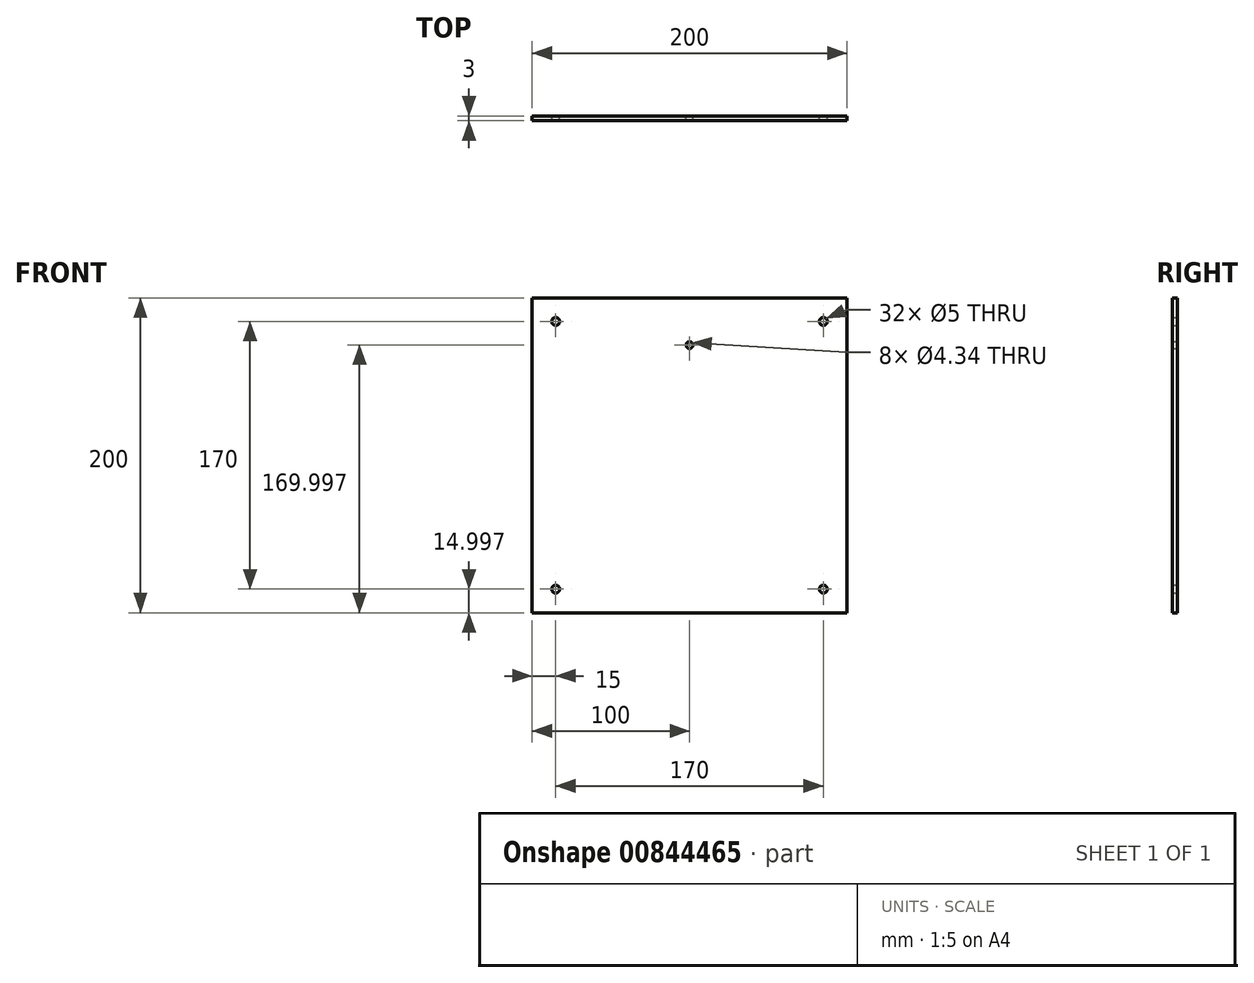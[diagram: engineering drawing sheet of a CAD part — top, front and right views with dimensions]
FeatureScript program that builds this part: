
annotation { "Feature Type Name" : "Feature", "Feature Type Description" : "" }
export const myFeature = defineFeature(function(context is Context, id is Id, definition is map)
    precondition{}
    {
        {
            var Q0;
            Q0=qCreatedBy(makeId("Front.planeOp"),FACE);
            var sketch = newSketch(context, id + "F0", { "sketchPlane" : qUnion([Q0])});
            skLineSegment(sketch, "E0.bottom", {"start": v(-100, 115.53) * mm, "end": v(100, 115.53) * mm});
            skLineSegment(sketch, "E0.top", {"start": v(-100, -84.47) * mm, "end": v(100, -84.47) * mm});
            skLineSegment(sketch, "E0.left", {"start": v(-100, 115.53) * mm, "end": v(-100, -84.47) * mm});
            skLineSegment(sketch, "E0.right", {"start": v(100, 115.53) * mm, "end": v(100, -84.47) * mm});
            skCircle(sketch, "E1", {"center": v(0, 85.53) * mm, "radius": 2.17 * mm});
            skCircle(sketch, "E2", {"center": v(-85, 100.53) * mm, "radius": 2.5 * mm});
            skCircle(sketch, "E3", {"center": v(85, 100.53) * mm, "radius": 2.5 * mm});
            skCircle(sketch, "E4", {"center": v(-85, -69.47) * mm, "radius": 2.5 * mm});
            skCircle(sketch, "E5", {"center": v(85, -69.47) * mm, "radius": 2.5 * mm});
            skSolve(sketch);
        }
        {
            var Q0;
            Q0=makeQuery(id+"F0.imprint","IMPRINT",FACE,{"disambiguationData":[TD([[makeQuery(id+"F0.imprint","IMPRINT",EDGE,{"derivedFrom":sQuery(id+"F0.wireOp",EDGE,"E0.bottom")}),-1.0]])]});
            extrude(context, id + "F1", {"entities" : qUnion([Q0]), "depth" : 3 * mm, "offsetDistance" : 25.4 * mm});
        }
    });
